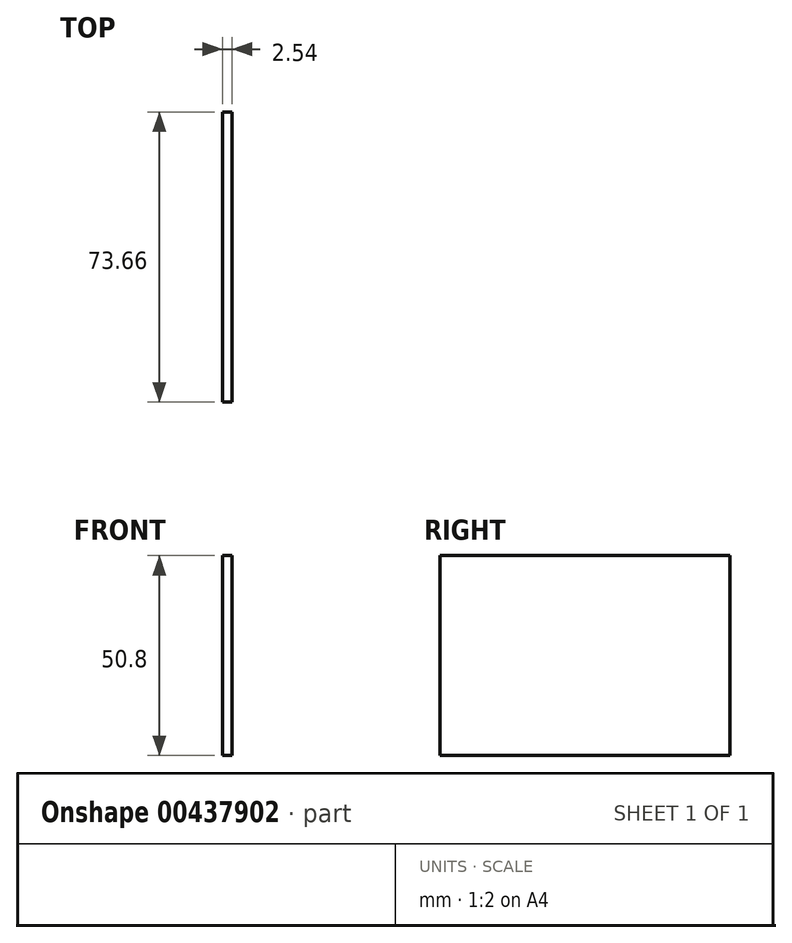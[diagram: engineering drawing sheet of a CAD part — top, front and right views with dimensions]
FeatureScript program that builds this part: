
annotation { "Feature Type Name" : "Feature", "Feature Type Description" : "" }
export const myFeature = defineFeature(function(context is Context, id is Id, definition is map)
    precondition{}
    {
        {
            var Q0;
            Q0=qCreatedBy(makeId("Right.planeOp"),FACE);
            var sketch = newSketch(context, id + "F0", { "sketchPlane" : qUnion([Q0])});
            skLineSegment(sketch, "E0.bottom", {"start": v(-42.22, 20.57) * mm, "end": v(31.44, 20.57) * mm});
            skLineSegment(sketch, "E0.top", {"start": v(-42.22, -30.23) * mm, "end": v(31.44, -30.23) * mm});
            skLineSegment(sketch, "E0.left", {"start": v(-42.22, 20.57) * mm, "end": v(-42.22, -30.23) * mm});
            skLineSegment(sketch, "E0.right", {"start": v(31.44, 20.57) * mm, "end": v(31.44, -30.23) * mm});
            skSolve(sketch);
        }
        {
            var Q0;
            Q0=makeQuery(id+"F0.imprint","IMPRINT",FACE,{"disambiguationData":[TD([[makeQuery(id+"F0.imprint","IMPRINT",EDGE,{"derivedFrom":sQuery(id+"F0.wireOp",EDGE,"E0.bottom")}),-1.0]])]});
            extrude(context, id + "F1", {"entities" : qUnion([Q0]), "depth" : 2.54 * mm});
        }
    });
